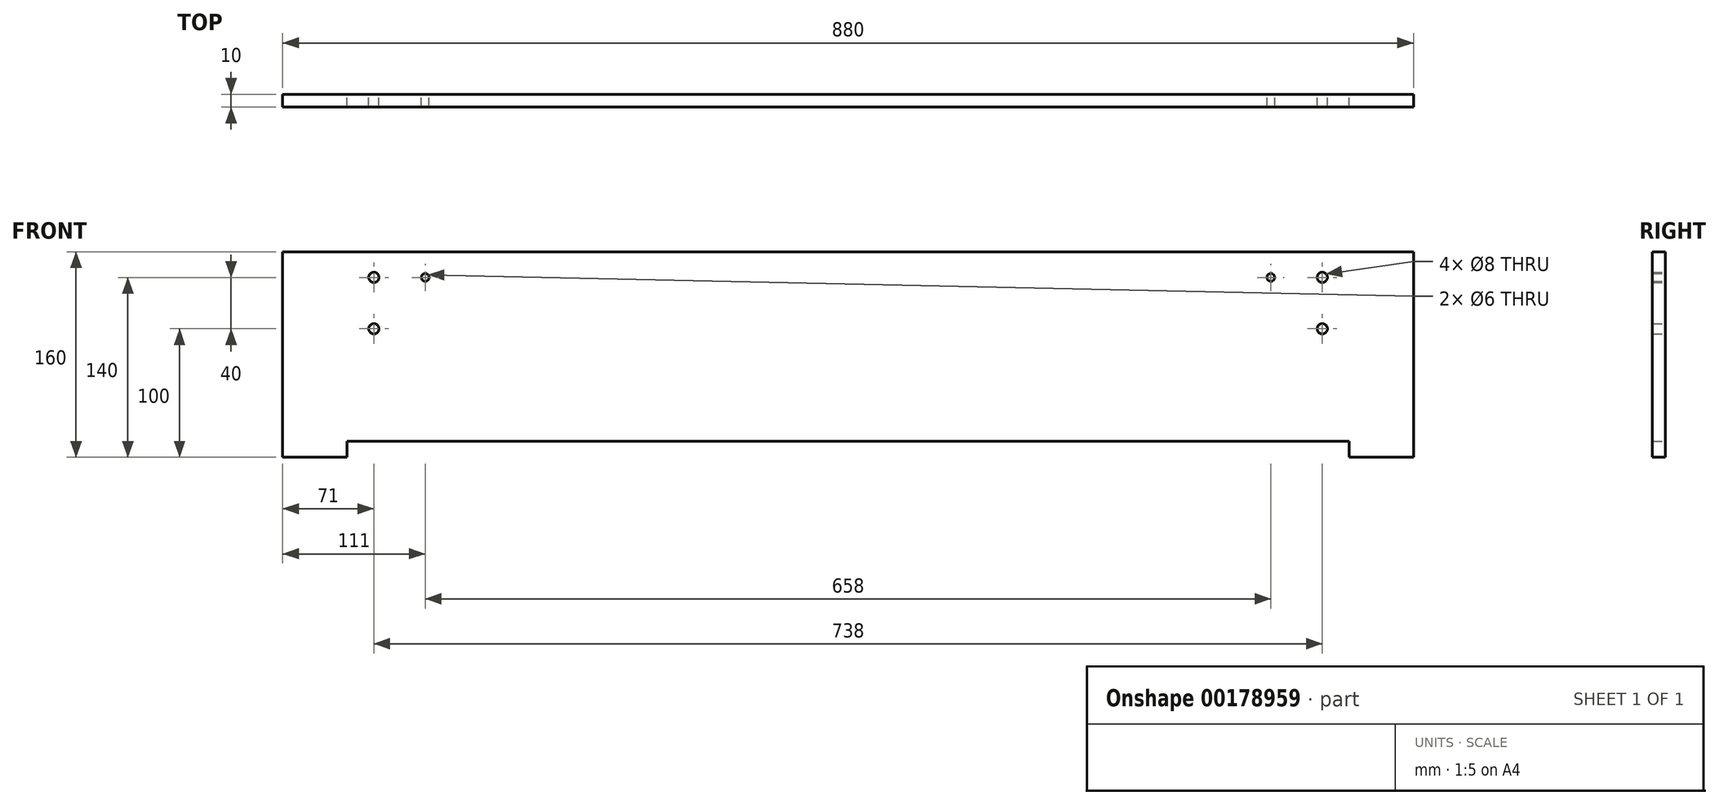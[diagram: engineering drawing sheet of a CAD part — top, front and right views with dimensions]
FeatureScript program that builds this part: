
annotation { "Feature Type Name" : "Feature", "Feature Type Description" : "" }
export const myFeature = defineFeature(function(context is Context, id is Id, definition is map)
    precondition{}
    {
        {
            var Q0;
            Q0=qCreatedBy(makeId("Front.planeOp"),FACE);
            var sketch = newSketch(context, id + "F0", { "sketchPlane" : qUnion([Q0])});
            skLineSegment(sketch, "E0.bottom", {"start": v(440, -80) * mm, "end": v(390, -80) * mm});
            skLineSegment(sketch, "E0.top", {"start": v(440, 80) * mm, "end": v(-440, 80) * mm});
            skLineSegment(sketch, "E0.left", {"start": v(440, -80) * mm, "end": v(440, 80) * mm});
            skLineSegment(sketch, "E0.right", {"start": v(-440, -80) * mm, "end": v(-440, 80) * mm});
            skPoint(sketch, "E0.middle", {"position": v(0, 0) * mm});
            skLineSegment(sketch, "E1", {"start": v(-390, -67.5) * mm, "end": v(-390, -80) * mm});
            skLineSegment(sketch, "E2", {"start": v(390, -67.5) * mm, "end": v(390, -80) * mm});
            skLineSegment(sketch, "E3", {"start": v(-390, -67.5) * mm, "end": v(390, -67.5) * mm});
            skLineSegment(sketch, "E4.trimOffspring", {"start": v(-390, -80) * mm, "end": v(-440, -80) * mm});
            skCircle(sketch, "E5", {"center": v(-369, 60) * mm, "radius": 4 * mm});
            skCircle(sketch, "E6", {"center": v(-369, 20) * mm, "radius": 4 * mm});
            skCircle(sketch, "E7", {"center": v(-329, 60) * mm, "radius": 3 * mm});
            skCircle(sketch, "E8", {"center": v(369, 60) * mm, "radius": 4 * mm});
            skCircle(sketch, "E9", {"center": v(369, 20) * mm, "radius": 4 * mm});
            skCircle(sketch, "E10", {"center": v(329, 60) * mm, "radius": 3 * mm});
            skSolve(sketch);
        }
        {
            var Q0;
            Q0=makeQuery(id+"F0.imprint","IMPRINT",FACE,{"disambiguationData":[TD([[makeQuery(id+"F0.imprint","IMPRINT",EDGE,{"derivedFrom":sQuery(id+"F0.wireOp",EDGE,"E0.bottom")}),-1.0]])]});
            extrude(context, id + "F1", {"entities" : qUnion([Q0]), "depth" : 10 * mm});
        }
    });
